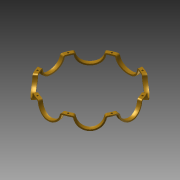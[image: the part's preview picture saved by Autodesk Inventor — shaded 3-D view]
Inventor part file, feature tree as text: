
AUTODESK INVENTOR PART (.ipt)
format: ipt  version: 2011 SP2 (Build 150309200, 309)  size: 305,664 bytes
history: native  units: mm
features: sketch x3, extrude x2, pattern_circular x2, revolve x1, fillet x1, shell x1
ambient origin geometry x8: Origin, YZ Plane, XZ Plane, XY Plane, X Axis, Y Axis, Z Axis, Center Point
bodies: Solid1 (feature_tree)
feature tree (10):
  extrude  "Extrusion1"  Depth=43.0mm
  revolve  "Revolution1"  [1 undecoded]
  fillet  "Fillet1"  Radius=12.0mm
  pattern_circular  "Circular Pattern1"  [2 undecoded]
  shell  "Shell1"  Thickness=90.0deg
  extrude  "Extrusion2"  Depth=2.0mm
  pattern_circular  "Circular Pattern2"  Count=8 Angle=360.0deg
  sketch  "Sketch1"  dims[d0=47.0mm d1=43.0mm]
  sketch  "Sketch2"  dims[d2=16.0mm d3=0.0mm d4=45.0mm d5=12.0mm]
  sketch  "Sketch3"  dims[d6=12.0mm d7=24.0mm d8=90.0deg d9=2.0mm d10=80.0mm d11=360.0deg d13=1.5mm d14=45.0mm d15=22.5deg d16=1.0mm d17=16.0mm d18=0.0mm d19=80.0mm d20=360.0deg]
note: 3 required parameter values undecoded (feature->parameter linkage not recoverable at this tier; creation-order binding heuristic only, values carry confidence <= 0.55)